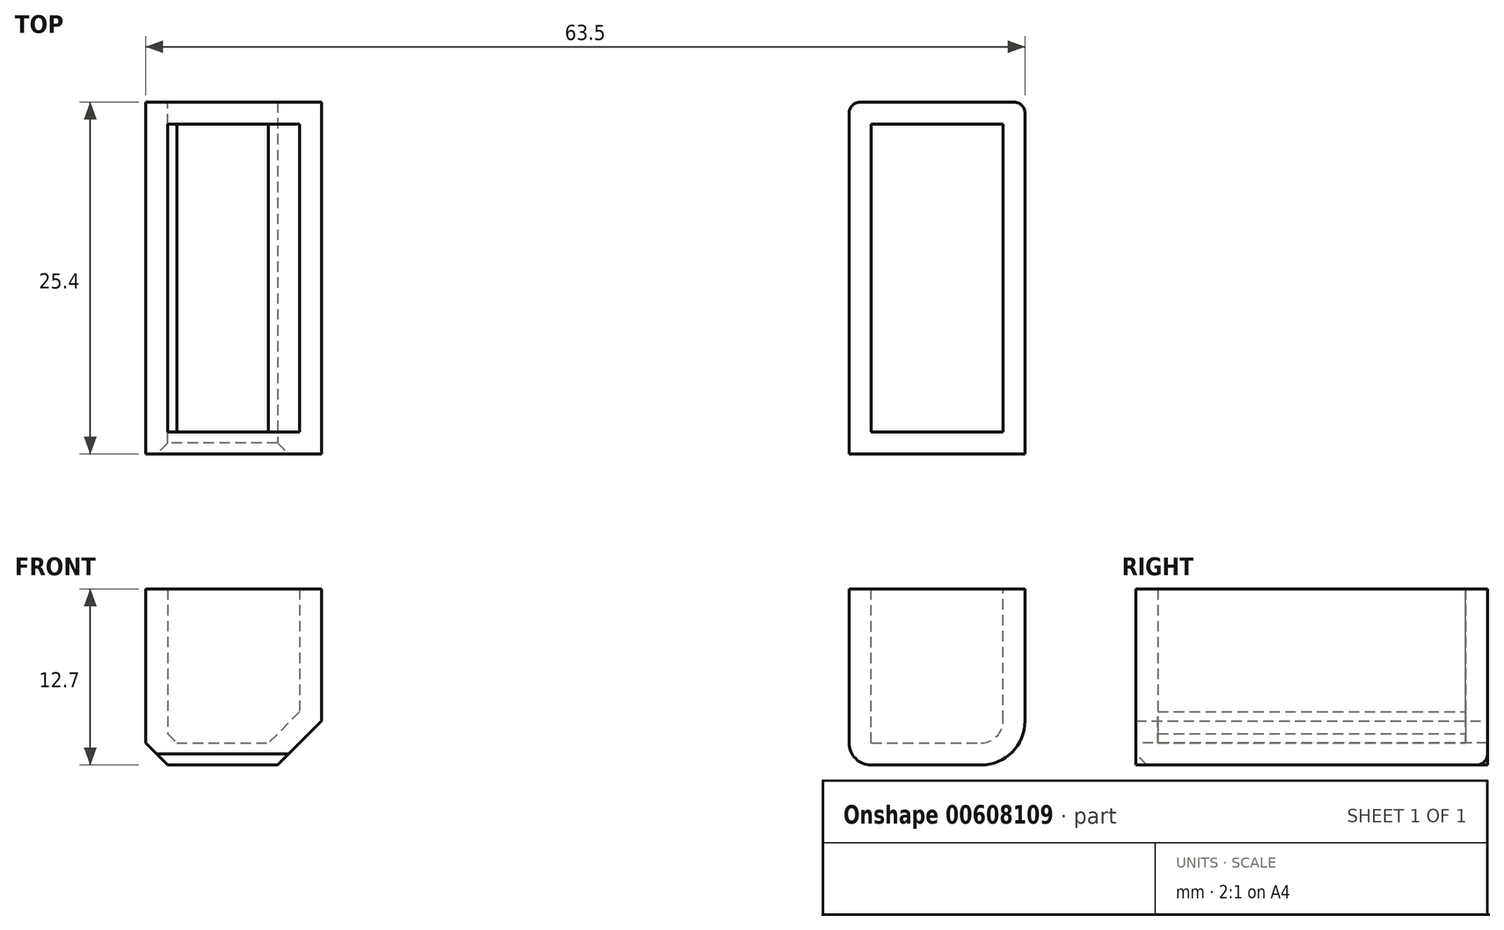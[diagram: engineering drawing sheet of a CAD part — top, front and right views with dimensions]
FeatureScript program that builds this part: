
annotation { "Feature Type Name" : "Feature", "Feature Type Description" : "" }
export const myFeature = defineFeature(function(context is Context, id is Id, definition is map)
    precondition{}
    {
        {
            var Q0;
            Q0=qCreatedBy(makeId("Top.planeOp"),FACE);
            var sketch = newSketch(context, id + "F0", { "sketchPlane" : qUnion([Q0])});
            skLineSegment(sketch, "E0.bottom", {"start": v(-24.22, 35.96) * mm, "end": v(-11.52, 35.96) * mm});
            skLineSegment(sketch, "E0.top", {"start": v(-24.22, 10.56) * mm, "end": v(-11.52, 10.56) * mm});
            skLineSegment(sketch, "E0.left", {"start": v(-24.22, 35.96) * mm, "end": v(-24.22, 10.56) * mm});
            skLineSegment(sketch, "E0.right", {"start": v(-11.52, 35.96) * mm, "end": v(-11.52, 10.56) * mm});
            skSolve(sketch);
        }
        {
            var Q0;
            Q0=makeQuery(id+"F0.imprint","IMPRINT",FACE,{"disambiguationData":[TD([[makeQuery(id+"F0.imprint","IMPRINT",EDGE,{"derivedFrom":sQuery(id+"F0.wireOp",EDGE,"E0.bottom")}),-1.0]])]});
            extrude(context, id + "F1", {"entities" : qUnion([Q0]), "depth" : 12.7 * mm, "offsetDistance" : 25.4 * mm});
        }
        {
            var Q0;
            Q0=makeQuery(id+"F1.opExtrude","SWEPT_BODY",BODY,{"disambiguationData":[OSD([sQuery(id+"F0.wireOp",EDGE,"E0.bottom"),sQuery(id+"F0.wireOp",EDGE,"E0.top"),sQuery(id+"F0.wireOp",EDGE,"E0.left"),sQuery(id+"F0.wireOp",EDGE,"E0.right")])]});
            transform(context, id + "F2", {"entities" : qUnion([Q0]), "transformType" : TransformType.TRANSLATION_3D, "dx" : 50.8 * mm, "dy" : 0 * mm, "dz" : 0 * mm, "makeCopy" : true});
        }
        {
            var Q0;
            Q0=makeQuery(id+"F1.opExtrude","CAP_EDGE",EDGE,{"disambiguationData":[OSD([sQuery(id+"F0.wireOp",EDGE,"E0.right")])],"isStart":true});
            chamfer(context, id + "F3", {"entities" : qUnion([Q0]), "width" : 3.17 * mm, "tangentPropagation" : true});
        }
        {
            var Q0;
            Q0=makeQuery(id+"F1.opExtrude","CAP_EDGE",EDGE,{"disambiguationData":[OSD([sQuery(id+"F0.wireOp",EDGE,"E0.left")])],"isStart":true});
            chamfer(context, id + "F4", {"entities" : qUnion([Q0]), "width" : 1.59 * mm, "tangentPropagation" : true});
        }
        {
            var Q0;
            Q0=makeQuery(id+"F1.opExtrude","CAP_EDGE",EDGE,{"disambiguationData":[OSD([sQuery(id+"F0.wireOp",EDGE,"E0.top")])],"isStart":true});
            chamfer(context, id + "F5", {"entities" : qUnion([Q0]), "width" : 0.8 * mm, "tangentPropagation" : true});
        }
        {
            var Q0;
            Q0=makeQuery(id+"F1.opExtrude","CAP_FACE",FACE,{"disambiguationData":[OSD([sQuery(id+"F0.wireOp",EDGE,"E0.bottom"),sQuery(id+"F0.wireOp",EDGE,"E0.top"),sQuery(id+"F0.wireOp",EDGE,"E0.left"),sQuery(id+"F0.wireOp",EDGE,"E0.right")])],"isStart":false});
            shell(context, id + "F6", {"entities" : qUnion([Q0]), "thickness" : 1.59 * mm});
        }
        {
            var Q0;
            Q0=makeQuery(id+"F2.opPattern","COPY",EDGE,{"derivedFrom":makeQuery(id+"F1.opExtrude","CAP_EDGE",EDGE,{"disambiguationData":[OSD([sQuery(id+"F0.wireOp",EDGE,"E0.right")])],"isStart":true}),"instanceName":"1"});
            fillet(context, id + "F7", {"entities" : qUnion([Q0]), "radius" : 3.17 * mm, "tangentPropagation" : true, "allowEdgeOverflow" : false});
        }
        {
            var Q0;
            Q0=makeQuery(id+"F2.opPattern","COPY",EDGE,{"derivedFrom":makeQuery(id+"F1.opExtrude","CAP_EDGE",EDGE,{"disambiguationData":[OSD([sQuery(id+"F0.wireOp",EDGE,"E0.left")])],"isStart":true}),"instanceName":"1"});
            fillet(context, id + "F8", {"entities" : qUnion([Q0]), "radius" : 1.59 * mm, "tangentPropagation" : true, "allowEdgeOverflow" : false});
        }
        {
            var Q0;
            Q0=makeQuery(id+"F2.opPattern","COPY",EDGE,{"derivedFrom":makeQuery(id+"F1.opExtrude","CAP_EDGE",EDGE,{"disambiguationData":[OSD([sQuery(id+"F0.wireOp",EDGE,"E0.bottom")])],"isStart":true}),"instanceName":"1"});
            fillet(context, id + "F9", {"entities" : qUnion([Q0]), "radius" : 0.8 * mm, "tangentPropagation" : true, "allowEdgeOverflow" : false});
        }
        {
            var Q0;
            Q0=makeQuery(id+"F2.opPattern","COPY",FACE,{"derivedFrom":makeQuery(id+"F1.opExtrude","CAP_FACE",FACE,{"disambiguationData":[OSD([sQuery(id+"F0.wireOp",EDGE,"E0.bottom"),sQuery(id+"F0.wireOp",EDGE,"E0.top"),sQuery(id+"F0.wireOp",EDGE,"E0.left"),sQuery(id+"F0.wireOp",EDGE,"E0.right")])],"isStart":false}),"instanceName":"1"});
            shell(context, id + "F10", {"entities" : qUnion([Q0]), "thickness" : 1.59 * mm});
        }
    });
